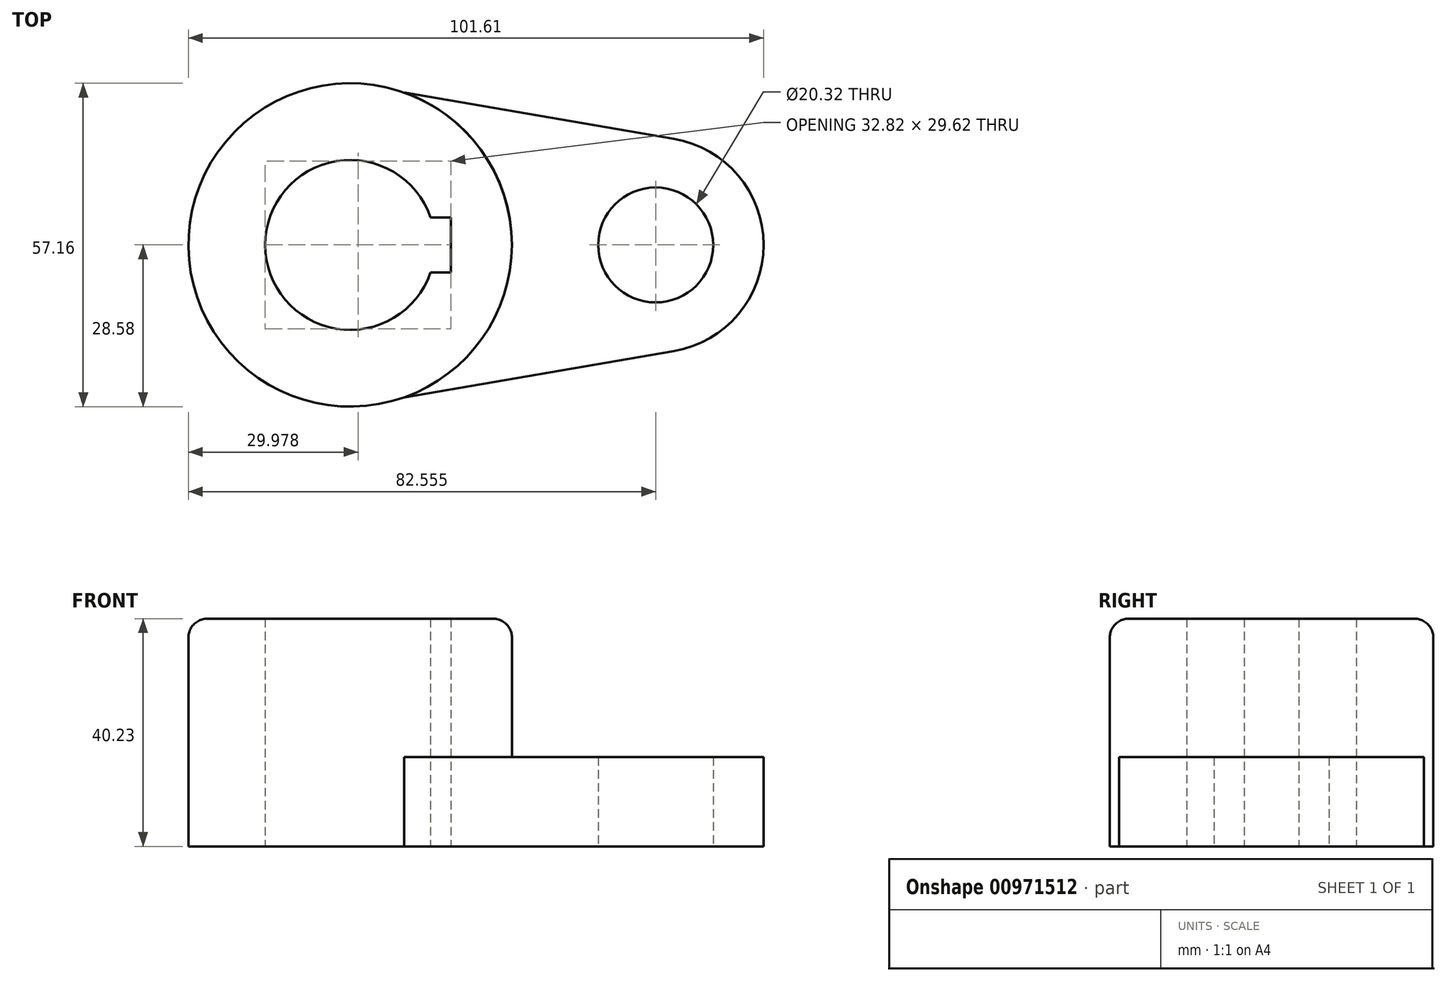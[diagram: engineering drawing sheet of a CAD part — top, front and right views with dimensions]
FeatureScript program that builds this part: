
annotation { "Feature Type Name" : "Feature", "Feature Type Description" : "" }
export const myFeature = defineFeature(function(context is Context, id is Id, definition is map)
    precondition{}
    {
        {
            var Q0;
            Q0=qCreatedBy(makeId("Top.planeOp"),FACE);
            var sketch = newSketch(context, id + "F0", { "sketchPlane" : qUnion([Q0])});
            skCircle(sketch, "E0", {"center": v(0, 0) * mm, "radius": 28.58 * mm});
            skArc(sketch, "E1", {"start": v(14.2, 4.85) * mm, "mid": v(-15.01, 0) * mm, "end": v(14.2, -4.85) * mm});
            skArc(sketch, "E2", {"start": v(57.2, -18.78) * mm, "mid": v(73.03, 0) * mm, "end": v(57.2, 18.78) * mm});
            skLineSegment(sketch, "E3", {"start": v(57.2, 18.78) * mm, "end": v(9.51, 26.95) * mm});
            skLineSegment(sketch, "E4", {"start": v(9.51, -26.95) * mm, "end": v(57.2, -18.78) * mm});
            skPoint(sketch, "E5.orphan", {"position": v(0, -28.58) * mm});
            skPoint(sketch, "E6.orphan", {"position": v(0, 28.58) * mm});
            skCircle(sketch, "E7", {"center": v(53.98, 0) * mm, "radius": 10.16 * mm});
            skLineSegment(sketch, "E8", {"start": v(14.2, 4.85) * mm, "end": v(17.8, 4.85) * mm});
            skLineSegment(sketch, "E9", {"start": v(17.8, 4.85) * mm, "end": v(17.8, -4.85) * mm});
            skLineSegment(sketch, "E10", {"start": v(17.8, -4.85) * mm, "end": v(14.2, -4.85) * mm});
            skCircle(sketch, "E11", {"center": v(0, 0) * mm, "radius": 24.93 * mm});
            skSolve(sketch);
        }
        {
            var Q0;
            Q0=makeQuery(id+"F0.imprint","IMPRINT",FACE,{"disambiguationData":[TD([[makeQuery(id+"F0.imprint","IMPRINT",EDGE,{"derivedFrom":sQuery(id+"F0.wireOp",EDGE,"E1")}),-1.0]])]});
            var Q1;
            Q1=makeQuery(id+"F0.imprint","IMPRINT",FACE,{"disambiguationData":[TD([[makeQuery(id+"F0.imprint","IMPRINT",EDGE,{"derivedFrom":sQuery(id+"F0.wireOp",EDGE,"E11")}),-1.0]])]});
            extrude(context, id + "F1", {"entities" : qUnion([Q0, Q1]), "depth" : 40.23 * mm, "offsetDistance" : 25.4 * mm});
        }
        {
            var Q0;
            Q0=makeQuery(id+"F0.imprint","IMPRINT",FACE,{"disambiguationData":[TD([[makeQuery(id+"F0.imprint","IMPRINT",EDGE,{"derivedFrom":sQuery(id+"F0.wireOp",EDGE,"E2")}),1.0]])]});
            var sketch = newSketch(context, id + "F2", { "sketchPlane" : qUnion([Q0])});
            skSolve(sketch);
        }
        {
            var Q0;
            Q0=makeQuery(id+"F2.imprint","IMPRINT",FACE,{"disambiguationData":[TD([[makeQuery(id+"F2.imprint","IMPRINT",EDGE,{"derivedFrom":makeQuery(id+"F0.imprint","IMPRINT",EDGE,{"derivedFrom":sQuery(id+"F0.wireOp",EDGE,"E2")})}),1.0]])]});
            extrude(context, id + "F3", {"entities" : qUnion([Q0]), "operationType" : NewBodyOperationType.ADD, "depth" : 15.77 * mm, "offsetDistance" : 25.4 * mm});
        }
        {
            var Q0;
            Q0=makeQuery(id+"F1.opExtrude","CAP_EDGE",EDGE,{"disambiguationData":[OSD([sQuery(id+"F0.wireOp",EDGE,"E0")])],"isStart":false});
            fillet(context, id + "F4", {"entities" : qUnion([Q0]), "radius" : 3.3 * mm, "tangentPropagation" : true, "allowEdgeOverflow" : false});
        }
    });
